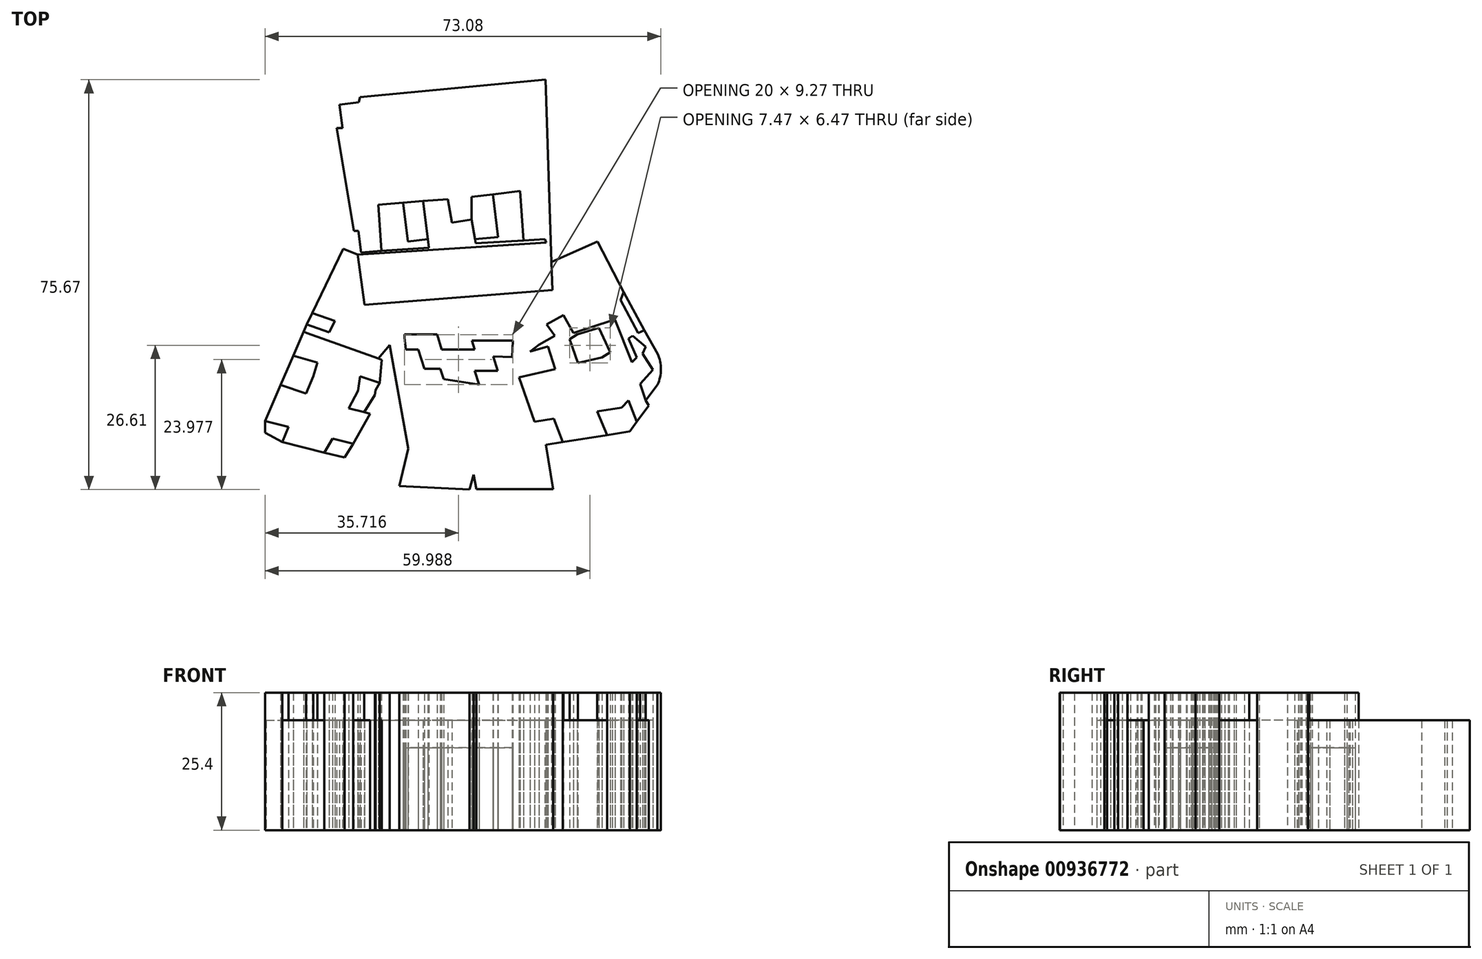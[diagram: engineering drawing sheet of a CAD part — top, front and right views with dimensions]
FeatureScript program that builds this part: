
annotation { "Feature Type Name" : "Feature", "Feature Type Description" : "" }
export const myFeature = defineFeature(function(context is Context, id is Id, definition is map)
    precondition{}
    {
        {
            var Q0;
            Q0=qCreatedBy(makeId("Top.planeOp"),FACE);
            var sketch = newSketch(context, id + "F0", { "sketchPlane" : qUnion([Q0])});
            skLineSegment(sketch, "E0", {"start": v(-49.5, -31.02) * mm, "end": v(-49.73, -31.47) * mm});
            skLineSegment(sketch, "E1", {"start": v(-49.73, -31.47) * mm, "end": v(-45.36, -32.58) * mm});
            skLineSegment(sketch, "E2", {"start": v(-45.36, -32.58) * mm, "end": v(-46.54, -35.32) * mm});
            skLineSegment(sketch, "E3", {"start": v(-46.54, -35.32) * mm, "end": v(-38.78, -37.3) * mm});
            skLineSegment(sketch, "E4", {"start": v(-38.78, -37.3) * mm, "end": v(-37.28, -34.71) * mm});
            skLineSegment(sketch, "E5", {"start": v(-37.28, -34.71) * mm, "end": v(-33.46, -35.68) * mm});
            skLineSegment(sketch, "E6", {"start": v(-33.46, -35.68) * mm, "end": v(-30.37, -30.11) * mm});
            skLineSegment(sketch, "E7", {"start": v(-30.37, -30.11) * mm, "end": v(-34.27, -29.12) * mm});
            skLineSegment(sketch, "E8", {"start": v(-34.27, -29.12) * mm, "end": v(-32.54, -25.88) * mm});
            skLineSegment(sketch, "E9", {"start": v(-32.54, -25.88) * mm, "end": v(-32.2, -23.22) * mm});
            skLineSegment(sketch, "E10", {"start": v(-32.2, -23.22) * mm, "end": v(-28.56, -24.45) * mm});
            skLineSegment(sketch, "E11", {"start": v(-36.8, -13.02) * mm, "end": v(-37.9, -15.08) * mm});
            skLineSegment(sketch, "E12", {"start": v(-28.56, -24.45) * mm, "end": v(-28.18, -20.15) * mm});
            skLineSegment(sketch, "E13", {"start": v(-28.18, -20.15) * mm, "end": v(-28.81, -19.88) * mm});
            skLineSegment(sketch, "E14", {"start": v(15.9, -9.11) * mm, "end": v(19.1, -15.19) * mm});
            skLineSegment(sketch, "E15", {"start": v(19.1, -15.19) * mm, "end": v(20.28, -14.68) * mm});
            skLineSegment(sketch, "E16", {"start": v(16.46, -7.67) * mm, "end": v(15.9, -9.11) * mm});
            skLineSegment(sketch, "E17", {"start": v(-28.81, -19.88) * mm, "end": v(-42, -15.22) * mm});
            skLineSegment(sketch, "E18", {"start": v(-28.56, -24.45) * mm, "end": v(-29.3, -25.75) * mm});
            skLineSegment(sketch, "E19", {"start": v(-29.3, -25.75) * mm, "end": v(-29.44, -26.67) * mm});
            skLineSegment(sketch, "E20", {"start": v(-29.44, -26.67) * mm, "end": v(-31.4, -29.85) * mm});
            skLineSegment(sketch, "E21", {"start": v(-49.5, -31.02) * mm, "end": v(-42, -13.63) * mm});
            skLineSegment(sketch, "E22", {"start": v(-49.73, -31.47) * mm, "end": v(-49.73, -33.6) * mm});
            skLineSegment(sketch, "E23", {"start": v(-49.73, -33.6) * mm, "end": v(-46.54, -35.32) * mm});
            skLineSegment(sketch, "E24", {"start": v(-33.46, -35.68) * mm, "end": v(-35, -38.18) * mm});
            skLineSegment(sketch, "E25", {"start": v(-35, -38.18) * mm, "end": v(-38.78, -37.3) * mm});
            skLineSegment(sketch, "E26", {"start": v(-35.3, 0.32) * mm, "end": v(-32.62, -0.74) * mm});
            skLineSegment(sketch, "E27", {"start": v(-32.62, -0.74) * mm, "end": v(-32.02, -0.34) * mm});
            skLineSegment(sketch, "E28", {"start": v(-36.47, 22.66) * mm, "end": v(-35.42, 22.66) * mm});
            skLineSegment(sketch, "E29", {"start": v(-35.42, 22.66) * mm, "end": v(-35.98, 26.92) * mm});
            skLineSegment(sketch, "E30", {"start": v(-35.98, 26.92) * mm, "end": v(-32.44, 27.38) * mm});
            skLineSegment(sketch, "E31", {"start": v(-32.44, 27.38) * mm, "end": v(-32.2, 28.33) * mm});
            skLineSegment(sketch, "E32", {"start": v(-32.2, 28.33) * mm, "end": v(2.04, 31.56) * mm});
            skLineSegment(sketch, "E33", {"start": v(3.31, -5.7) * mm, "end": v(8.98, -3.46) * mm});
            skLineSegment(sketch, "E34", {"start": v(8.98, -3.46) * mm, "end": v(11.66, 1.7) * mm});
            skLineSegment(sketch, "E35", {"start": v(11.66, 1.7) * mm, "end": v(3.19, -2.1) * mm});
            skLineSegment(sketch, "E36", {"start": v(8.98, -3.46) * mm, "end": v(14.39, -12.84) * mm});
            skLineSegment(sketch, "E37", {"start": v(14.39, -12.84) * mm, "end": v(11.92, -14.27) * mm});
            skLineSegment(sketch, "E38", {"start": v(11.92, -14.27) * mm, "end": v(7.9, -15.5) * mm});
            skLineSegment(sketch, "E39", {"start": v(7.9, -15.5) * mm, "end": v(6.52, -16.38) * mm});
            skLineSegment(sketch, "E40", {"start": v(6.52, -16.38) * mm, "end": v(2.5, -17.66) * mm});
            skLineSegment(sketch, "E41", {"start": v(2.5, -17.66) * mm, "end": v(-0.8, -18.64) * mm});
            skLineSegment(sketch, "E42", {"start": v(-0.8, -18.64) * mm, "end": v(-4.14, -19.68) * mm});
            skLineSegment(sketch, "E43", {"start": v(-4.14, -19.68) * mm, "end": v(0, -31.62) * mm});
            skLineSegment(sketch, "E44", {"start": v(0, -31.62) * mm, "end": v(1.3, -35.97) * mm});
            skLineSegment(sketch, "E45", {"start": v(1.3, -35.97) * mm, "end": v(13.4, -34.05) * mm});
            skLineSegment(sketch, "E46", {"start": v(13.4, -34.05) * mm, "end": v(17.59, -33.35) * mm});
            skLineSegment(sketch, "E47", {"start": v(17.59, -33.35) * mm, "end": v(21.09, -28.62) * mm});
            skLineSegment(sketch, "E48", {"start": v(21.09, -28.62) * mm, "end": v(20.54, -27.67) * mm});
            skLineSegment(sketch, "E49", {"start": v(13.4, -34.05) * mm, "end": v(11.59, -29.7) * mm});
            skLineSegment(sketch, "E50", {"start": v(11.59, -29.7) * mm, "end": v(16.09, -28.98) * mm});
            skLineSegment(sketch, "E51", {"start": v(16.09, -28.98) * mm, "end": v(17.32, -27.67) * mm});
            skLineSegment(sketch, "E52", {"start": v(17.32, -27.67) * mm, "end": v(18.87, -31.62) * mm});
            skLineSegment(sketch, "E53", {"start": v(0, -31.62) * mm, "end": v(3.6, -31.05) * mm});
            skLineSegment(sketch, "E54", {"start": v(3.6, -31.05) * mm, "end": v(5.25, -35.34) * mm});
            skLineSegment(sketch, "E55", {"start": v(2.5, -17.66) * mm, "end": v(3.83, -21.88) * mm});
            skLineSegment(sketch, "E56", {"start": v(3.83, -21.88) * mm, "end": v(-2.86, -23.38) * mm});
            skLineSegment(sketch, "E57", {"start": v(6.52, -16.38) * mm, "end": v(8.03, -20.73) * mm});
            skLineSegment(sketch, "E58", {"start": v(8.03, -20.73) * mm, "end": v(12.48, -19.73) * mm});
            skLineSegment(sketch, "E59", {"start": v(12.48, -19.73) * mm, "end": v(14, -18.76) * mm});
            skLineSegment(sketch, "E60", {"start": v(14, -18.76) * mm, "end": v(11.92, -14.27) * mm});
            skLineSegment(sketch, "E61", {"start": v(20.54, -27.67) * mm, "end": v(19.5, -24.63) * mm});
            skLineSegment(sketch, "E62", {"start": v(19.5, -24.63) * mm, "end": v(21.86, -22.01) * mm});
            skLineSegment(sketch, "E63", {"start": v(21.86, -22.01) * mm, "end": v(19.98, -19.03) * mm});
            skLineSegment(sketch, "E64", {"start": v(19.98, -19.03) * mm, "end": v(20.54, -17.78) * mm});
            skLineSegment(sketch, "E65", {"start": v(20.54, -17.78) * mm, "end": v(18.1, -15.74) * mm});
            skLineSegment(sketch, "E66", {"start": v(18.1, -15.74) * mm, "end": v(17.38, -16.21) * mm});
            skLineSegment(sketch, "E67", {"start": v(17.38, -16.21) * mm, "end": v(18.9, -19.74) * mm});
            skLineSegment(sketch, "E68", {"start": v(18.9, -19.74) * mm, "end": v(18.01, -20.62) * mm});
            skLineSegment(sketch, "E69", {"start": v(18.01, -20.62) * mm, "end": v(14.85, -12.83) * mm});
            skLineSegment(sketch, "E70", {"start": v(14.85, -12.83) * mm, "end": v(14.39, -12.84) * mm});
            skArc(sketch, "E71", {"start": v(22.7, -24.77) * mm, "mid": v(23.35, -21.92) * mm, "end": v(22.75, -19.07) * mm});
            skLineSegment(sketch, "E72", {"start": v(22.7, -24.77) * mm, "end": v(20.54, -27.67) * mm});
            skLineSegment(sketch, "E73", {"start": v(11.66, 1.7) * mm, "end": v(16.46, -7.67) * mm});
            skLineSegment(sketch, "E74", {"start": v(-28.81, -19.88) * mm, "end": v(-26.74, -17.41) * mm});
            skLineSegment(sketch, "E75", {"start": v(-24.01, -15.5) * mm, "end": v(-17.98, -15.5) * mm});
            skLineSegment(sketch, "E76", {"start": v(-17.98, -15.5) * mm, "end": v(-17.11, -18.25) * mm});
            skLineSegment(sketch, "E77", {"start": v(-17.11, -18.25) * mm, "end": v(-11.05, -18.25) * mm});
            skLineSegment(sketch, "E78", {"start": v(-11.05, -18.25) * mm, "end": v(-11.57, -16.62) * mm});
            skLineSegment(sketch, "E79", {"start": v(-11.57, -16.62) * mm, "end": v(-4.01, -16.62) * mm});
            skLineSegment(sketch, "E80", {"start": v(-4.01, -16.62) * mm, "end": v(-4.14, -19.68) * mm});
            skLineSegment(sketch, "E81", {"start": v(-4.14, -19.68) * mm, "end": v(-7.61, -19.54) * mm});
            skLineSegment(sketch, "E82", {"start": v(-7.61, -19.54) * mm, "end": v(-6.77, -22.21) * mm});
            skLineSegment(sketch, "E83", {"start": v(-6.77, -22.21) * mm, "end": v(-11.05, -22.21) * mm});
            skLineSegment(sketch, "E84", {"start": v(-11.05, -22.21) * mm, "end": v(-10.24, -24.77) * mm});
            skLineSegment(sketch, "E85", {"start": v(-10.24, -24.77) * mm, "end": v(-16.78, -23.7) * mm});
            skLineSegment(sketch, "E86", {"start": v(-16.78, -23.7) * mm, "end": v(-17.36, -21.85) * mm});
            skLineSegment(sketch, "E87", {"start": v(-17.36, -21.85) * mm, "end": v(-20.3, -21.85) * mm});
            skLineSegment(sketch, "E88", {"start": v(-20.3, -21.85) * mm, "end": v(-21.43, -18.25) * mm});
            skLineSegment(sketch, "E89", {"start": v(-21.43, -18.25) * mm, "end": v(-23.71, -18.25) * mm});
            skLineSegment(sketch, "E90", {"start": v(-23.71, -18.25) * mm, "end": v(-24.01, -16.06) * mm});
            skLineSegment(sketch, "E91", {"start": v(-24.01, -16.06) * mm, "end": v(-24.01, -15.5) * mm});
            skLineSegment(sketch, "E92", {"start": v(2.04, 31.56) * mm, "end": v(3.31, -7.3) * mm});
            skLineSegment(sketch, "E93", {"start": v(3.31, -7.3) * mm, "end": v(-31.33, -10) * mm});
            skLineSegment(sketch, "E94", {"start": v(-32.62, -0.74) * mm, "end": v(-31.33, -10) * mm});
            skLineSegment(sketch, "E95", {"start": v(-32.62, -0.74) * mm, "end": v(3.02, 1.55) * mm});
            skLineSegment(sketch, "E96", {"start": v(-36.47, 22.66) * mm, "end": v(-33.33, 3.63) * mm});
            skLineSegment(sketch, "E97", {"start": v(-33.33, 3.63) * mm, "end": v(-32.51, 3.63) * mm});
            skLineSegment(sketch, "E98", {"start": v(-32.51, 3.63) * mm, "end": v(-32.02, -0.34) * mm});
            skLineSegment(sketch, "E99", {"start": v(-19.5, 0.56) * mm, "end": v(-20.58, 9.2) * mm});
            skLineSegment(sketch, "E100", {"start": v(-20.58, 9.2) * mm, "end": v(-15.97, 9.5) * mm});
            skLineSegment(sketch, "E101", {"start": v(-15.97, 9.5) * mm, "end": v(-15.25, 5.14) * mm});
            skLineSegment(sketch, "E102", {"start": v(-15.25, 5.14) * mm, "end": v(-11.57, 5.75) * mm});
            skLineSegment(sketch, "E103", {"start": v(-11.57, 5.75) * mm, "end": v(-10.84, 1.33) * mm});
            skLineSegment(sketch, "E104", {"start": v(-10.84, 1.33) * mm, "end": v(1.94, 2.15) * mm});
            skLineSegment(sketch, "E105", {"start": v(1.94, 2.15) * mm, "end": v(2.16, 1.5) * mm});
            skLineSegment(sketch, "E106", {"start": v(-11.57, 5.75) * mm, "end": v(-11.57, 9.91) * mm});
            skLineSegment(sketch, "E107", {"start": v(-11.57, 9.91) * mm, "end": v(-2.62, 11.03) * mm});
            skLineSegment(sketch, "E108", {"start": v(-2.62, 11.03) * mm, "end": v(-2.04, 1.9) * mm});
            skLineSegment(sketch, "E109", {"start": v(-28.24, 0) * mm, "end": v(-28.79, 8.49) * mm});
            skLineSegment(sketch, "E110", {"start": v(-28.79, 8.49) * mm, "end": v(-20.58, 9.2) * mm});
            skLineSegment(sketch, "E111", {"start": v(-24.24, 8.88) * mm, "end": v(-23.34, 1.69) * mm});
            skLineSegment(sketch, "E112", {"start": v(-23.34, 1.69) * mm, "end": v(-19.7, 2.14) * mm});
            skLineSegment(sketch, "E113", {"start": v(-10.98, 2.14) * mm, "end": v(-6.7, 2.51) * mm});
            skLineSegment(sketch, "E114", {"start": v(-6.7, 2.51) * mm, "end": v(-7.69, 10.4) * mm});
            skLineSegment(sketch, "E115", {"start": v(-32.02, -0.34) * mm, "end": v(-19.5, 0.56) * mm});
            skLineSegment(sketch, "E116", {"start": v(2.25, -13.63) * mm, "end": v(3.74, -15.74) * mm});
            skLineSegment(sketch, "E117", {"start": v(3.74, -15.74) * mm, "end": v(0.84, -17.34) * mm});
            skLineSegment(sketch, "E118", {"start": v(0.84, -17.34) * mm, "end": v(-0.8, -18.64) * mm});
            skLineSegment(sketch, "E119", {"start": v(2.25, -13.63) * mm, "end": v(5.35, -11.91) * mm});
            skLineSegment(sketch, "E120", {"start": v(5.35, -11.91) * mm, "end": v(7.18, -15.22) * mm});
            skLineSegment(sketch, "E121", {"start": v(7.18, -15.22) * mm, "end": v(14.39, -12.84) * mm});
            skLineSegment(sketch, "E122", {"start": v(-35.3, 0.32) * mm, "end": v(-42, -13.63) * mm});
            skLineSegment(sketch, "E123", {"start": v(-39.88, -9.22) * mm, "end": v(-25.04, -14.46) * mm});
            skLineSegment(sketch, "E124", {"start": v(-25.04, -14.46) * mm, "end": v(-26.74, -17.41) * mm});
            skLineSegment(sketch, "E125", {"start": v(-25.04, -14.46) * mm, "end": v(-24.35, -9.46) * mm});
            skLineSegment(sketch, "E126", {"start": v(-42, -15.22) * mm, "end": v(-42.57, -14.98) * mm});
            skLineSegment(sketch, "E127", {"start": v(-36.8, -13.02) * mm, "end": v(-41, -11.54) * mm});
            skLineSegment(sketch, "E128", {"start": v(-42, -13.63) * mm, "end": v(-37.9, -15.08) * mm});
            skLineSegment(sketch, "E129", {"start": v(-26.74, -17.41) * mm, "end": v(-23.27, -36.54) * mm});
            skLineSegment(sketch, "E130", {"start": v(-23.27, -36.54) * mm, "end": v(-24.92, -43.46) * mm});
            skLineSegment(sketch, "E131", {"start": v(-24.92, -43.46) * mm, "end": v(-11.96, -44.1) * mm});
            skLineSegment(sketch, "E132", {"start": v(-11.96, -44.1) * mm, "end": v(-11.24, -41.4) * mm});
            skLineSegment(sketch, "E133", {"start": v(-11.24, -41.4) * mm, "end": v(-10.72, -44.03) * mm});
            skLineSegment(sketch, "E134", {"start": v(-10.72, -44.03) * mm, "end": v(3.43, -44.03) * mm});
            skLineSegment(sketch, "E135", {"start": v(3.43, -44.03) * mm, "end": v(2.13, -35.84) * mm});
            skLineSegment(sketch, "E136", {"start": v(-14, -8.65) * mm, "end": v(-17.55, -16.88) * mm});
            skLineSegment(sketch, "E137", {"start": v(-25.04, -14.46) * mm, "end": v(-24.01, -15.5) * mm});
            skLineSegment(sketch, "E138", {"start": v(-23.71, -18.25) * mm, "end": v(-24.28, -30.96) * mm});
            skLineSegment(sketch, "E139", {"start": v(-24.28, -30.96) * mm, "end": v(-10.24, -24.77) * mm});
            skLineSegment(sketch, "E140", {"start": v(-10.24, -24.77) * mm, "end": v(-11.24, -41.4) * mm});
            skLineSegment(sketch, "E141", {"start": v(-23.27, -36.54) * mm, "end": v(-11.24, -41.4) * mm});
            skLineSegment(sketch, "E142", {"start": v(-11.24, -41.4) * mm, "end": v(1.3, -35.97) * mm});
            skLineSegment(sketch, "E143", {"start": v(-28.24, 0) * mm, "end": v(-28.24, -0.07) * mm});
            skLineSegment(sketch, "E144", {"start": v(3.31, -5.7) * mm, "end": v(3.26, -5.72) * mm});
            skLineSegment(sketch, "E145", {"start": v(3.19, -2.1) * mm, "end": v(3.14, -2.11) * mm});
            skLineSegment(sketch, "E146", {"start": v(16.46, -7.67) * mm, "end": v(20.28, -14.68) * mm});
            skLineSegment(sketch, "E147", {"start": v(-44.47, -19.37) * mm, "end": v(-40.04, -20.7) * mm});
            skLineSegment(sketch, "E148", {"start": v(-40.04, -20.7) * mm, "end": v(-40.79, -23.2) * mm});
            skLineSegment(sketch, "E149", {"start": v(-40.79, -23.2) * mm, "end": v(-42.16, -26.38) * mm});
            skLineSegment(sketch, "E150", {"start": v(-42.16, -26.38) * mm, "end": v(-46.82, -24.82) * mm});
            skLineSegment(sketch, "E151", {"start": v(20.28, -14.68) * mm, "end": v(22.75, -19.07) * mm});
            skSolve(sketch);
        }
        {
            var Q0;
            Q0=makeQuery(id+"F0.imprint","IMPRINT",FACE,{"disambiguationData":[TD([[makeQuery(id+"F0.imprint","IMPRINT",EDGE,{"derivedFrom":sQuery(id+"F0.wireOp",EDGE,"E37")}),1.0]])]});
            var Q1;
            Q1=makeQuery(id+"F0.imprint","IMPRINT",FACE,{"disambiguationData":[TD([[makeQuery(id+"F0.imprint","IMPRINT",EDGE,{"derivedFrom":sQuery(id+"F0.wireOp",EDGE,"E14")}),1.0]])]});
            var Q2;
            Q2=makeQuery(id+"F0.imprint","IMPRINT",FACE,{"disambiguationData":[TD([[makeQuery(id+"F0.imprint","IMPRINT",EDGE,{"derivedFrom":sQuery(id+"F0.wireOp",EDGE,"E37")}),-1.0]])]});
            var Q3;
            {var subQ4=sQuery(id+"F0.wireOp",EDGE,"E0");Q3=makeQuery(id+"F0.imprint","IMPRINT",FACE,{"disambiguationData":[TD([[makeQuery(id+"F0.imprint","IMPRINT",EDGE,{"derivedFrom":subQ4}),1.0]])]});}
            var Q4;
            Q4=makeQuery(id+"F0.imprint","IMPRINT",FACE,{"disambiguationData":[TD([[makeQuery(id+"F0.imprint","IMPRINT",EDGE,{"derivedFrom":sQuery(id+"F0.wireOp",EDGE,"E11")}),-1.0]])]});
            var Q5;
            Q5=makeQuery(id+"F0.imprint","IMPRINT",FACE,{"disambiguationData":[TD([[makeQuery(id+"F0.imprint","IMPRINT",EDGE,{"derivedFrom":sQuery(id+"F0.wireOp",EDGE,"E28")}),-1.0]])]});
            var Q6;
            {var subQ9=sQuery(id+"F0.wireOp",EDGE,"E94");Q6=makeQuery(id+"F0.imprint","IMPRINT",FACE,{"disambiguationData":[TD([[makeQuery(id+"F0.imprint","IMPRINT",EDGE,{"derivedFrom":subQ9}),1.0]])]});}
            extrude(context, id + "F1", {"entities" : qUnion([Q0, Q1, Q2, Q3, Q4, Q5, Q6]), "depth" : 20.32 * mm, "offsetDistance" : 25.4 * mm});
        }
        {
            var Q0;
            {var subQ2=sQuery(id+"F0.wireOp",EDGE,"E139");Q0=makeQuery(id+"F0.imprint","IMPRINT",FACE,{"disambiguationData":[TD([[makeQuery(id+"F0.imprint","IMPRINT",EDGE,{"derivedFrom":subQ2}),-1.0]])]});}
            var Q1;
            {var subQ3=sQuery(id+"F0.wireOp",EDGE,"E44");Q1=makeQuery(id+"F0.imprint","IMPRINT",FACE,{"disambiguationData":[TD([[makeQuery(id+"F0.imprint","IMPRINT",EDGE,{"derivedFrom":subQ3}),-1.0]])]});}
            var Q2;
            Q2=makeQuery(id+"F0.imprint","IMPRINT",FACE,{"disambiguationData":[TD([[makeQuery(id+"F0.imprint","IMPRINT",EDGE,{"derivedFrom":sQuery(id+"F0.wireOp",EDGE,"E85")}),1.0]])]});
            var Q3;
            Q3=makeQuery(id+"F0.imprint","IMPRINT",FACE,{"disambiguationData":[TD([[makeQuery(id+"F0.imprint","IMPRINT",EDGE,{"derivedFrom":sQuery(id+"F0.wireOp",EDGE,"E11")}),1.0]])]});
            var Q4;
            {var subQ4=sQuery(id+"F0.wireOp",EDGE,"E26");Q4=makeQuery(id+"F0.imprint","IMPRINT",FACE,{"disambiguationData":[TD([[makeQuery(id+"F0.imprint","IMPRINT",EDGE,{"derivedFrom":subQ4}),-1.0]])]});}
            var Q5;
            {var subQ4=sQuery(id+"F0.wireOp",EDGE,"E75");Q5=makeQuery(id+"F0.imprint","IMPRINT",FACE,{"disambiguationData":[TD([[makeQuery(id+"F0.imprint","IMPRINT",EDGE,{"derivedFrom":subQ4}),1.0]])]});}
            var Q6;
            Q6=makeQuery(id+"F0.imprint","IMPRINT",FACE,{"disambiguationData":[TD([[makeQuery(id+"F0.imprint","IMPRINT",EDGE,{"derivedFrom":sQuery(id+"F0.wireOp",EDGE,"E90")}),1.0]])]});
            var Q7;
            Q7=makeQuery(id+"F0.imprint","IMPRINT",FACE,{"disambiguationData":[TD([[makeQuery(id+"F0.imprint","IMPRINT",EDGE,{"derivedFrom":sQuery(id+"F0.wireOp",EDGE,"E130")}),1.0]])]});
            var Q8;
            Q8=makeQuery(id+"F0.imprint","IMPRINT",FACE,{"disambiguationData":[TD([[makeQuery(id+"F0.imprint","IMPRINT",EDGE,{"derivedFrom":sQuery(id+"F0.wireOp",EDGE,"E133")}),1.0]])]});
            var Q9;
            Q9=makeQuery(id+"F0.imprint","IMPRINT",FACE,{"disambiguationData":[TD([[makeQuery(id+"F0.imprint","IMPRINT",EDGE,{"derivedFrom":sQuery(id+"F0.wireOp",EDGE,"E33")}),-1.0]])]});
            var Q10;
            Q10=makeQuery(id+"F0.imprint","IMPRINT",FACE,{"disambiguationData":[TD([[makeQuery(id+"F0.imprint","IMPRINT",EDGE,{"derivedFrom":sQuery(id+"F0.wireOp",EDGE,"E33")}),1.0]])]});
            var Q11;
            {var subQ1=sQuery(id+"F0.wireOp",EDGE,"E8");Q11=makeQuery(id+"F0.imprint","IMPRINT",FACE,{"disambiguationData":[TD([[makeQuery(id+"F0.imprint","IMPRINT",EDGE,{"derivedFrom":subQ1}),-1.0]])]});}
            var Q12;
            Q12=makeQuery(id+"F0.imprint","IMPRINT",FACE,{"disambiguationData":[TD([[makeQuery(id+"F0.imprint","IMPRINT",EDGE,{"derivedFrom":sQuery(id+"F0.wireOp",EDGE,"E1")}),-1.0]])]});
            var Q13;
            Q13=makeQuery(id+"F0.imprint","IMPRINT",FACE,{"disambiguationData":[TD([[makeQuery(id+"F0.imprint","IMPRINT",EDGE,{"derivedFrom":sQuery(id+"F0.wireOp",EDGE,"E4")}),-1.0]])]});
            var Q14;
            {var subQ1=sQuery(id+"F0.wireOp",EDGE,"E46");Q14=makeQuery(id+"F0.imprint","IMPRINT",FACE,{"disambiguationData":[TD([[makeQuery(id+"F0.imprint","IMPRINT",EDGE,{"derivedFrom":subQ1}),1.0]])]});}
            var Q15;
            {var subQ1=sQuery(id+"F0.wireOp",EDGE,"E44");Q15=makeQuery(id+"F0.imprint","IMPRINT",FACE,{"disambiguationData":[TD([[makeQuery(id+"F0.imprint","IMPRINT",EDGE,{"derivedFrom":subQ1}),1.0]])]});}
            var Q16;
            Q16=makeQuery(id+"F0.imprint","IMPRINT",FACE,{"disambiguationData":[TD([[makeQuery(id+"F0.imprint","IMPRINT",EDGE,{"derivedFrom":sQuery(id+"F0.wireOp",EDGE,"E41")}),1.0]])]});
            var Q17;
            Q17=makeQuery(id+"F0.imprint","IMPRINT",FACE,{"disambiguationData":[TD([[makeQuery(id+"F0.imprint","IMPRINT",EDGE,{"derivedFrom":sQuery(id+"F0.wireOp",EDGE,"E38")}),1.0]])]});
            var Q18;
            Q18=makeQuery(id+"F0.imprint","IMPRINT",FACE,{"disambiguationData":[TD([[makeQuery(id+"F0.imprint","IMPRINT",EDGE,{"derivedFrom":sQuery(id+"F0.wireOp",EDGE,"E14")}),-1.0]])]});
            var Q19;
            {var subQ0=sQuery(id+"F0.wireOp",EDGE,"E147");Q19=makeQuery(id+"F0.imprint","IMPRINT",FACE,{"disambiguationData":[TD([[makeQuery(id+"F0.imprint","IMPRINT",EDGE,{"derivedFrom":subQ0}),-1.0]])]});}
            var Q20;
            {var subQ0=sQuery(id+"F0.wireOp",EDGE,"E108");Q20=makeQuery(id+"F0.imprint","IMPRINT",FACE,{"disambiguationData":[TD([[makeQuery(id+"F0.imprint","IMPRINT",EDGE,{"derivedFrom":subQ0}),-1.0]])]});}
            var Q21;
            {var subQ1=sQuery(id+"F0.wireOp",EDGE,"E109");Q21=makeQuery(id+"F0.imprint","IMPRINT",FACE,{"disambiguationData":[TD([[makeQuery(id+"F0.imprint","IMPRINT",EDGE,{"derivedFrom":subQ1}),-1.0]])]});}
            extrude(context, id + "F2", {"entities" : qUnion([Q0, Q1, Q2, Q3, Q4, Q5, Q6, Q7, Q8, Q9, Q10, Q11, Q12, Q13, Q14, Q15, Q16, Q17, Q18, Q19, Q20, Q21]), "depth" : 25.4 * mm, "offsetDistance" : 25.4 * mm});
        }
        {
            var Q0;
            {var subQ2=sQuery(id+"F0.wireOp",EDGE,"E106");Q0=makeQuery(id+"F0.imprint","IMPRINT",FACE,{"disambiguationData":[TD([[makeQuery(id+"F0.imprint","IMPRINT",EDGE,{"derivedFrom":subQ2}),-1.0]])]});}
            var Q1;
            {var subQ4=sQuery(id+"F0.wireOp",EDGE,"E111");Q1=makeQuery(id+"F0.imprint","IMPRINT",FACE,{"disambiguationData":[TD([[makeQuery(id+"F0.imprint","IMPRINT",EDGE,{"derivedFrom":subQ4}),1.0]])]});}
            var Q2;
            {var subQ0=sQuery(id+"F0.wireOp",EDGE,"E75");Q2=makeQuery(id+"F0.imprint","IMPRINT",FACE,{"disambiguationData":[TD([[makeQuery(id+"F0.imprint","IMPRINT",EDGE,{"derivedFrom":subQ0}),-1.0]])]});}
            extrude(context, id + "F3", {"entities" : qUnion([Q0, Q1, Q2]), "depth" : 15.24 * mm, "offsetDistance" : 25.4 * mm});
        }
    });
